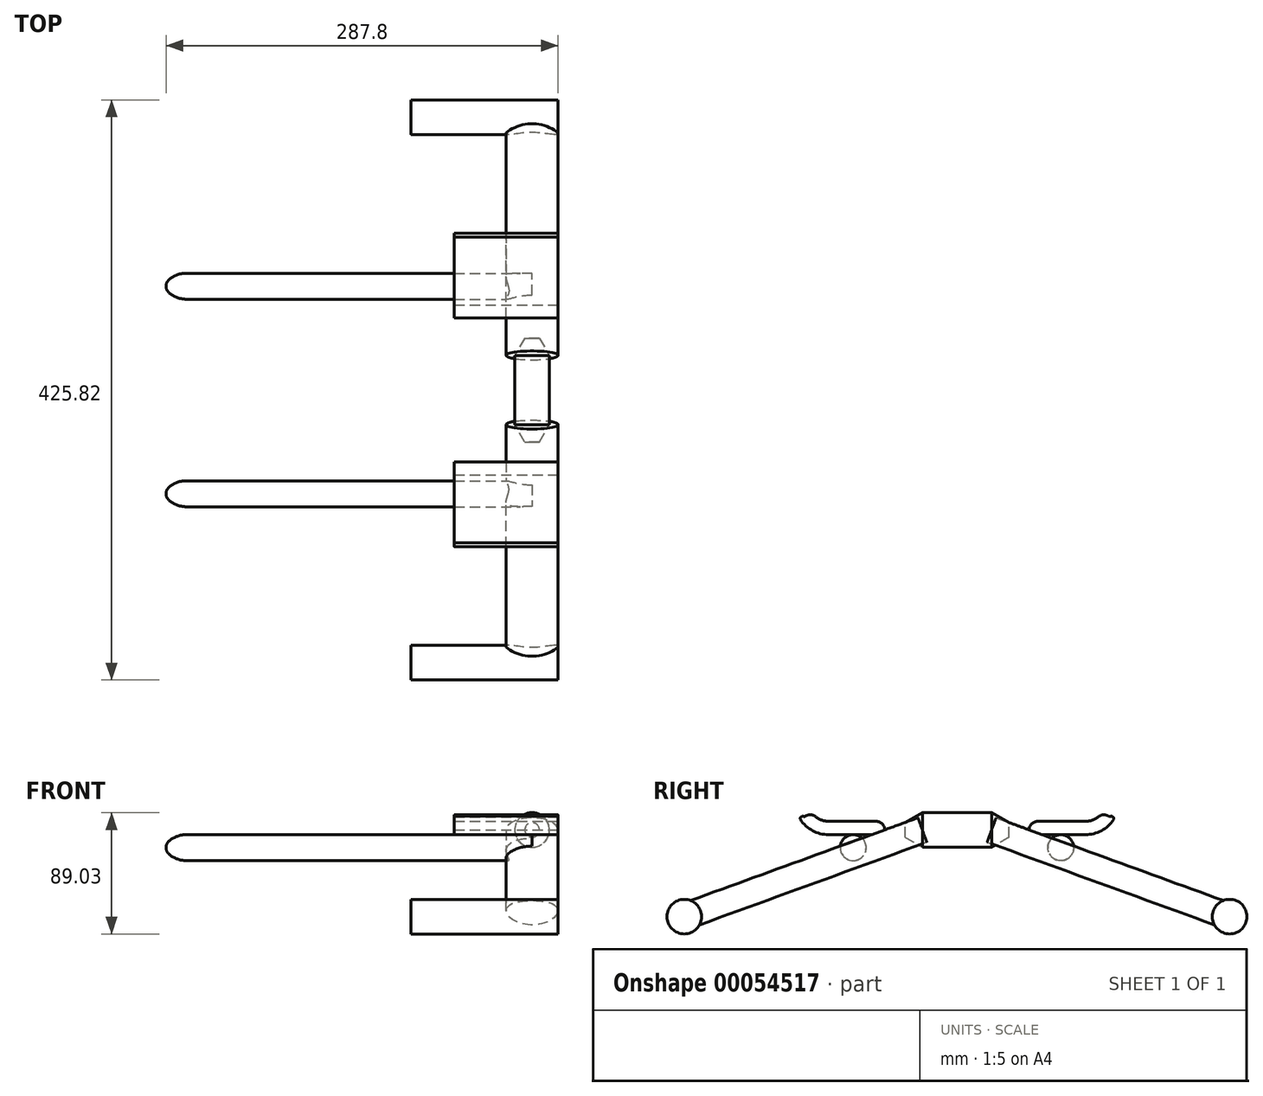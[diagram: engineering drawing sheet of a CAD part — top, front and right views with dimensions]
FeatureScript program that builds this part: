
annotation { "Feature Type Name" : "Feature", "Feature Type Description" : "" }
export const myFeature = defineFeature(function(context is Context, id is Id, definition is map)
    precondition{}
    {
        {
            var Q0;
            Q0=qCreatedBy(makeId("Front.planeOp"),FACE);
            var sketch = newSketch(context, id + "F0", { "sketchPlane" : qUnion([Q0])});
            skEllipse(sketch, "E0", {"center": v(0, 0) * mm, "majorRadius": 19.05 * mm, "minorRadius": 9.53 * mm, "majorAxis": v(1, 0)});
            skSolve(sketch);
        }
        {
            var Q0;
            Q0=makeQuery(id+"F0.imprint","IMPRINT",FACE,{"disambiguationData":[TD([[makeQuery(id+"F0.imprint","IMPRINT",EDGE,{"derivedFrom":sQuery(id+"F0.wireOp",EDGE,"E0")}),1.0]])]});
            extrude(context, id + "F1", {"entities" : qUnion([Q0]), "depth" : 177.8 * mm});
        }
        {
            var Q0;
            Q0=qCreatedBy(makeId("Right.planeOp"),FACE);
            var sketch = newSketch(context, id + "F2", { "sketchPlane" : qUnion([Q0])});
            skCircle(sketch, "E1", {"center": v(8.23, 0) * mm, "radius": 12.7 * mm});
            skSolve(sketch);
        }
        {
            var Q0;
            Q0=makeQuery(id+"F2.imprint","IMPRINT",FACE,{"disambiguationData":[TD([[makeQuery(id+"F2.imprint","IMPRINT",EDGE,{"derivedFrom":sQuery(id+"F2.wireOp",EDGE,"E1")}),1.0]])]});
            extrude(context, id + "F3", {"entities" : qUnion([Q0]), "operationType" : NewBodyOperationType.ADD, "depth" : 19.05 * mm, "hasSecondDirection" : true, "secondDirectionOppositeDirection" : true, "secondDirectionDepth" : 88.9 * mm});
        }
        {
            var Q0;
            Q0=qCreatedBy(makeId("Top.planeOp"),FACE);
            var sketch = newSketch(context, id + "F4", { "sketchPlane" : qUnion([Q0])});
            skLineSegment(sketch, "E2", {"start": v(-88.9, 20.93) * mm, "end": v(-88.9, 8.23) * mm});
            skLineSegment(sketch, "E3.0", {"start": v(-88.9, 20.93) * mm, "end": v(-88.9, -4.47) * mm});
            skLineSegment(sketch, "E4", {"start": v(-88.9, 8.23) * mm, "end": v(-109.45, 8.23) * mm});
            skArc(sketch, "E5", {"start": v(-88.9, 20.93) * mm, "mid": v(-99.27, 18.72) * mm, "end": v(-107.83, 12.46) * mm});
            skPoint(sketch, "E6.visualSharp", {"position": v(-110.9, 8.23) * mm});
            skArc(sketch, "E6.filletArc", {"start": v(-107.83, 12.46) * mm, "mid": v(-109.03, 10.5) * mm, "end": v(-109.45, 8.23) * mm});
            skSolve(sketch);
        }
        {
            var Q0;
            Q0=sQuery(id+"F4.wireOp",EDGE,"E5");
            var Q1;
            Q1=sQuery(id+"F4.wireOp",EDGE,"E6.filletArc");
            var Q2;
            Q2=sQuery(id+"F4.wireOp",EDGE,"E4");
            revolve(context, id + "F5", {"bodyType" : ToolBodyType.SURFACE, "surfaceEntities" : qUnion([Q0, Q1]), "axis" : qUnion([Q2]), "revolveType" : RevolveType.FULL});
        }
        {
            var Q0;
            Q0=makeQuery(id+"F3.opExtrude","CAP_FACE",FACE,{"disambiguationData":[OSD([sQuery(id+"F2.wireOp",EDGE,"E1")])],"isStart":true});
            cPlane(context, id + "F6", {"entities" : qUnion([Q0]), "cplaneType" : CPlaneType.OFFSET, "offset" : 0 * mm, "width" : 152.4 * mm, "height" : 152.4 * mm});
        }
        {
            var Q0;
            Q0=makeQuery(id+"F1.opExtrude","CAP_FACE",FACE,{"disambiguationData":[OSD([sQuery(id+"F0.wireOp",EDGE,"E0")])],"isStart":false});
            var sketch = newSketch(context, id + "F7", { "sketchPlane" : qUnion([Q0])});
            skLineSegment(sketch, "E7", {"start": v(-19.05, 0) * mm, "end": v(19.05, 0) * mm, "construction": true});
            skSolve(sketch);
        }
        {
            var Q0;
            Q0=makeQuery(id+"F5.opRevolve","SWEPT_BODY",BODY,{"disambiguationData":[OSD([sQuery(id+"F4.wireOp",EDGE,"E6.filletArc")])]});
            var Q1;
            Q1=makeQuery(id+"F1.opExtrude","SWEPT_BODY",BODY,{"disambiguationData":[OSD([sQuery(id+"F0.wireOp",EDGE,"E0")])]});
            var Q2;
            Q2=sQuery(id+"F7.wireOp",EDGE,"E7");
            transform(context, id + "F8", {"entities" : qUnion([Q0, Q1]), "transformType" : TransformType.ROTATION, "transformAxis" : qUnion([Q2]), "angle" : 20 * degree, "oppositeDirection" : true, "makeCopy" : false});
        }
        {
            var Q0;
            Q0=qCreatedBy(makeId("Front.planeOp"),FACE);
            cPlane(context, id + "F9", {"entities" : qUnion([Q0]), "cplaneType" : CPlaneType.OFFSET, "offset" : 203.2 * mm, "width" : 152.4 * mm, "height" : 152.4 * mm});
        }
        {
            var Q0;
            Q0=makeQuery(id+"F1.opExtrude","SWEPT_BODY",BODY,{"disambiguationData":[OSD([sQuery(id+"F0.wireOp",EDGE,"E0")])]});
            var Q1;
            Q1=makeQuery(id+"F5.opRevolve","SWEPT_BODY",BODY,{"disambiguationData":[OSD([sQuery(id+"F4.wireOp",EDGE,"E6.filletArc")])]});
            var Q2;
            Q2=qCreatedBy(id+"F9.planeOp",FACE);
            mirror(context, id + "F10", {"entities" : qUnion([Q0, Q1]), "mirrorPlane" : qUnion([Q2])});
        }
        {
            var Q0;
            Q0=qCreatedBy(id+"F9.planeOp",FACE);
            var sketch = newSketch(context, id + "F11", { "sketchPlane" : qUnion([Q0])});
            skCircle(sketch, "E8", {"center": v(0, 0) * mm, "radius": 12.7 * mm});
            skSolve(sketch);
        }
        {
            var Q0;
            Q0 = qSketchRegion(id + "F11", true);
            extrude(context, id + "F12", {"entities" : qUnion([Q0]), "depth" : 38.1 * mm, "hasSecondDirection" : true, "secondDirectionOppositeDirection" : true, "secondDirectionDepth" : 38.1 * mm});
        }
        {
            var Q0;
            Q0=makeQuery(id+"F12.opExtrude","SWEPT_FACE",FACE,{"disambiguationData":[OSD([sQuery(id+"F11.wireOp",EDGE,"E8")])]});
            chamfer(context, id + "F13", {"entities" : qUnion([Q0]), "chamferType" : ChamferType.OFFSET_ANGLE, "width" : 12.7 * mm, "oppositeDirection" : false, "angle" : 30 * degree});
        }
        {
            var Q0;
            Q0=qCreatedBy(id+"F9.planeOp",FACE);
            cPlane(context, id + "F14", {"entities" : qUnion([Q0]), "cplaneType" : CPlaneType.OFFSET, "offset" : 76.2 * mm, "width" : 152.4 * mm, "height" : 152.4 * mm});
        }
        {
            var Q0;
            Q0=qCreatedBy(id+"F14.planeOp",FACE);
            var sketch = newSketch(context, id + "F15", { "sketchPlane" : qUnion([Q0])});
            skLineSegment(sketch, "E9", {"start": v(0, -3.42) * mm, "end": v(-254, -3.42) * mm});
            skLineSegment(sketch, "E10", {"start": v(-254, -3.42) * mm, "end": v(-254, -12.94) * mm});
            skLineSegment(sketch, "E11", {"start": v(0, -12.94) * mm, "end": v(0, -3.42) * mm});
            skLineSegment(sketch, "E12", {"start": v(40.74, -12.94) * mm, "end": v(-254, -12.94) * mm, "construction": true});
            skArc(sketch, "E13", {"start": v(-254, -3.42) * mm, "mid": v(-260.74, -4.65) * mm, "end": v(-266.6, -8.18) * mm});
            skPoint(sketch, "E14.visualSharp", {"position": v(-270.5, -12.94) * mm});
            skArc(sketch, "E14.filletArc", {"start": v(-266.6, -8.18) * mm, "mid": v(-268.19, -10.33) * mm, "end": v(-268.75, -12.94) * mm});
            skPoint(sketch, "E15.orphan", {"position": v(0, -22.47) * mm});
            skLineSegment(sketch, "E16", {"start": v(0, -12.94) * mm, "end": v(-268.75, -12.94) * mm});
            skSolve(sketch);
        }
        {
            var Q0;
            Q0 = qSketchRegion(id + "F15", true);
            var Q1;
            Q1=sQuery(id+"F15.wireOp",EDGE,"E12");
            revolve(context, id + "F16", {"operationType" : NewBodyOperationType.ADD, "entities" : qUnion([Q0]), "axis" : qUnion([Q1]), "revolveType" : RevolveType.FULL});
        }
        {
            var Q0;
            Q0=makeQuery(id+"F10.opPattern","COPY",BODY,{"derivedFrom":makeQuery(id+"F1.opExtrude","SWEPT_BODY",BODY,{"disambiguationData":[OSD([sQuery(id+"F0.wireOp",EDGE,"E0")])]}),"instanceName":"1"});
            var Q1;
            Q1=qCreatedBy(id+"F9.planeOp",FACE);
            mirror(context, id + "F17", {"entities" : qUnion([Q0]), "mirrorPlane" : qUnion([Q1])});
        }
        {
            var Q0;
            Q0=makeQuery(id+"F10.opPattern","COPY",FACE,{"derivedFrom":makeQuery(id+"F3.opExtrude","CAP_FACE",FACE,{"disambiguationData":[OSD([sQuery(id+"F2.wireOp",EDGE,"E1")])],"isStart":false}),"instanceName":"1"});
            cPlane(context, id + "F18", {"entities" : qUnion([Q0]), "cplaneType" : CPlaneType.OFFSET, "offset" : 0 * mm, "width" : 152.4 * mm, "height" : 152.4 * mm});
        }
        {
            var Q0;
            Q0=qCreatedBy(id+"F18.planeOp",FACE);
            var sketch = newSketch(context, id + "F19", { "sketchPlane" : qUnion([Q0])});
            skLineSegment(sketch, "E17", {"start": v(-297.5, -3.42) * mm, "end": v(-265.55, -3.42) * mm});
            skLineSegment(sketch, "E18", {"start": v(-265.55, -3.42) * mm, "end": v(-256.18, 0) * mm});
            skArc(sketch, "E19", {"start": v(-297.5, -3.42) * mm, "mid": v(-309.23, -0.45) * mm, "end": v(-318.14, 7.72) * mm});
            skArc(sketch, "E20.0", {"start": v(-297.52, 0.04) * mm, "mid": v(-307.6, 2.58) * mm, "end": v(-315.3, 9.58) * mm});
            skLineSegment(sketch, "E20.1", {"start": v(-297.52, 0.04) * mm, "end": v(-256.18, 0) * mm});
            skLineSegment(sketch, "E21", {"start": v(-317.75, 9.54) * mm, "end": v(-317.08, 9.96) * mm});
            skPoint(sketch, "E22.visualSharp", {"position": v(-315.98, 10.66) * mm});
            skArc(sketch, "E22.filletArc", {"start": v(-315.3, 9.58) * mm, "mid": v(-316.12, 10.13) * mm, "end": v(-317.08, 9.96) * mm});
            skPoint(sketch, "E23.visualSharp", {"position": v(-318.84, 8.85) * mm});
            skArc(sketch, "E23.filletArc", {"start": v(-317.75, 9.54) * mm, "mid": v(-318.33, 8.71) * mm, "end": v(-318.14, 7.72) * mm});
            skArc(sketch, "E24.0", {"start": v(-297.5, 6.39) * mm, "mid": v(-302.53, 7.25) * mm, "end": v(-306.98, 9.75) * mm});
            skLineSegment(sketch, "E24.1", {"start": v(-297.5, 6.39) * mm, "end": v(-262.52, 6.36) * mm});
            skLineSegment(sketch, "E25", {"start": v(-315.3, 9.58) * mm, "end": v(-314.5, 10.11) * mm});
            skLineSegment(sketch, "E26", {"start": v(-256.18, 0) * mm, "end": v(-256.18, 0) * mm});
            skPoint(sketch, "E27.visualSharp", {"position": v(-310.02, 13.1) * mm});
            skArc(sketch, "E27.filletArc", {"start": v(-306.98, 9.75) * mm, "mid": v(-310.68, 11.17) * mm, "end": v(-314.5, 10.11) * mm});
            skPoint(sketch, "E28.visualSharp", {"position": v(-256.17, 6.35) * mm});
            skArc(sketch, "E28.filletArc", {"start": v(-256.18, 0) * mm, "mid": v(-258.03, 4.5) * mm, "end": v(-262.52, 6.36) * mm});
            skSolve(sketch);
        }
        {
            var Q0;
            Q0 = qSketchRegion(id + "F19", true);
            extrude(context, id + "F20", {"entities" : qUnion([Q0]), "oppositeDirection" : true, "depth" : 76.2 * mm});
        }
        {
            var Q0;
            Q0=makeQuery(id+"F20.opExtrude","SWEPT_BODY",BODY,{"disambiguationData":[OSD([sQuery(id+"F19.wireOp",EDGE,"E17"),sQuery(id+"F19.wireOp",EDGE,"E18"),sQuery(id+"F19.wireOp",EDGE,"E19"),sQuery(id+"F19.wireOp",EDGE,"E21"),sQuery(id+"F19.wireOp",EDGE,"E22.filletArc"),sQuery(id+"F19.wireOp",EDGE,"E23.filletArc"),sQuery(id+"F19.wireOp",EDGE,"E24.0"),sQuery(id+"F19.wireOp",EDGE,"E24.1"),sQuery(id+"F19.wireOp",EDGE,"E25"),sQuery(id+"F19.wireOp",EDGE,"E27.filletArc"),sQuery(id+"F19.wireOp",EDGE,"E28.filletArc")])]});
            var Q1;
            Q1=qCreatedBy(id+"F9.planeOp",FACE);
            mirror(context, id + "F21", {"entities" : qUnion([Q0]), "mirrorPlane" : qUnion([Q1])});
        }
        {
            var Q0;
            Q0=qCreatedBy(id+"F9.planeOp",FACE);
            cPlane(context, id + "F22", {"entities" : qUnion([Q0]), "cplaneType" : CPlaneType.OFFSET, "offset" : 200.66 * mm, "width" : 152.4 * mm, "height" : 152.4 * mm});
        }
    });
